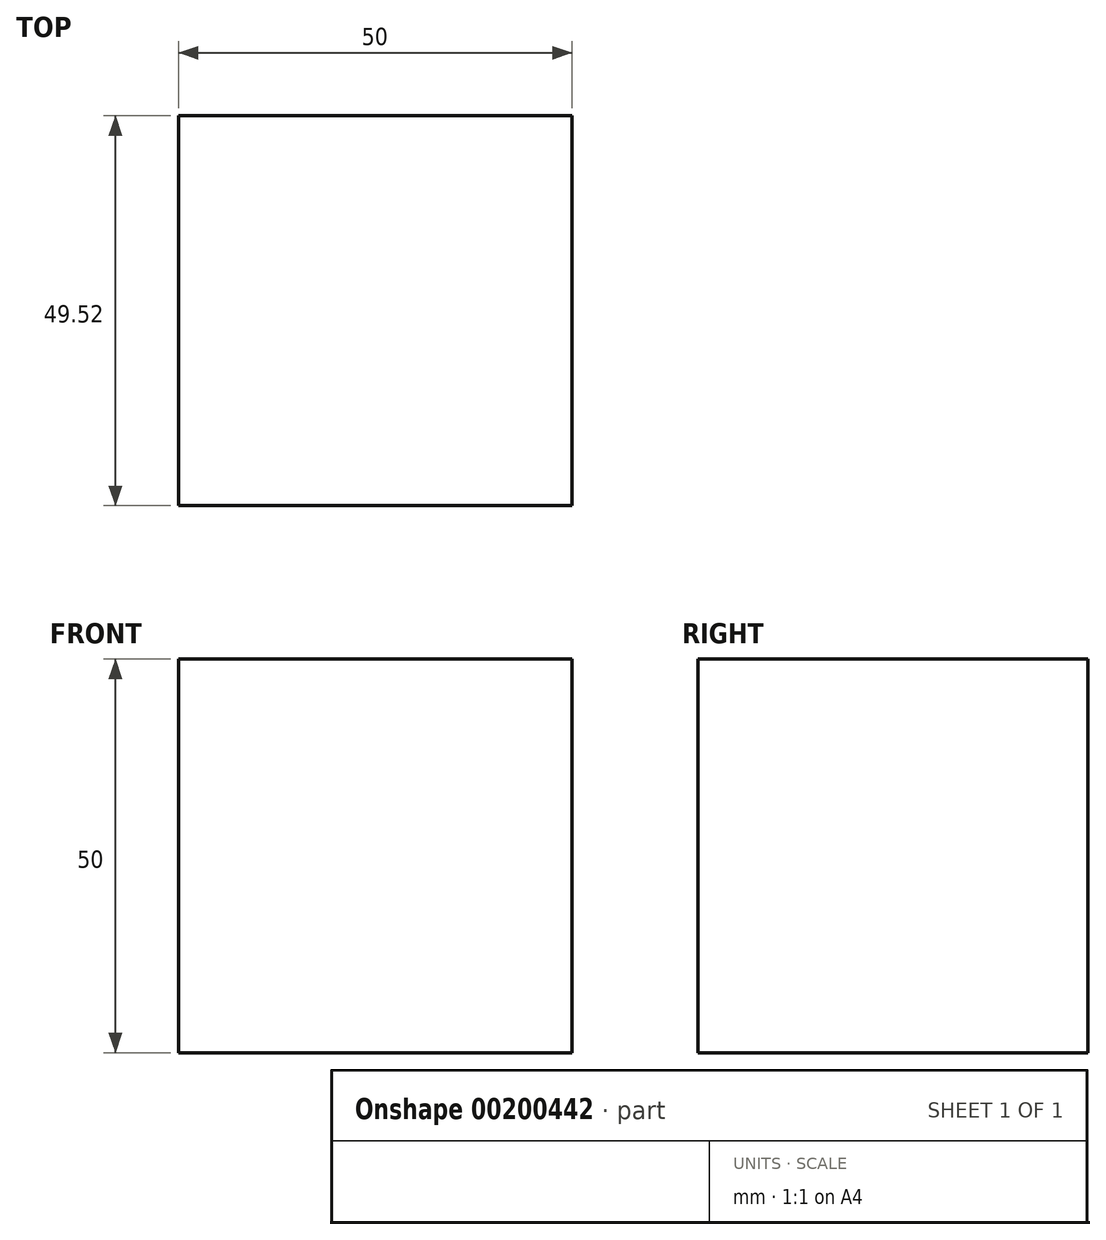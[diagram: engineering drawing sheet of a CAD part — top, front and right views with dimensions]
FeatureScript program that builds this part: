
annotation { "Feature Type Name" : "Feature", "Feature Type Description" : "" }
export const myFeature = defineFeature(function(context is Context, id is Id, definition is map)
    precondition{}
    {
        {
            var Q0;
            Q0=qCreatedBy(makeId("Top.planeOp"),FACE);
            var sketch = newSketch(context, id + "F0", { "sketchPlane" : qUnion([Q0])});
            skLineSegment(sketch, "E0.bottom", {"start": v(-25, 24.76) * mm, "end": v(25, 24.76) * mm});
            skLineSegment(sketch, "E0.top", {"start": v(-25, -24.76) * mm, "end": v(25, -24.76) * mm});
            skLineSegment(sketch, "E0.left", {"start": v(-25, 24.76) * mm, "end": v(-25, -24.76) * mm});
            skLineSegment(sketch, "E0.right", {"start": v(25, 24.76) * mm, "end": v(25, -24.76) * mm});
            skPoint(sketch, "E0.middle", {"position": v(0, 0) * mm});
            skSolve(sketch);
        }
        {
            var Q0;
            Q0 = qSketchRegion(id + "F0", true);
            extrude(context, id + "F1", {"entities" : qUnion([Q0]), "depth" : 50 * mm});
        }
    });
